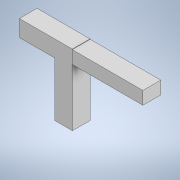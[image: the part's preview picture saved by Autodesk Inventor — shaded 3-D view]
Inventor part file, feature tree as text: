
AUTODESK INVENTOR PART (.ipt)
format: ipt  version: 2021.1 (Build 251245000, 245)  size: 110,592 bytes
history: native  units: in
note: dims shown in document units (in); Inventor stores cm internally (conversion verified against a paired STEP export)
features: extrude x3, sketch x3
ambient origin geometry x8: Origin, YZ Plane, XZ Plane, XY Plane, X Axis, Y Axis, Z Axis, Center Point
bodies: Solid1 (feature_tree)
feature tree (6):
  extrude  "Extrusion1"  Depth=4.0in TaperAngle=0.0deg
  extrude  "Extrusion2"  Depth=2.0in TaperAngle=0.0deg
  extrude  "Extrusion3"  [1 undecoded]
  sketch  "Sketch1"  dims[d0=1.0in d1=4.0in d2=0.0in]
  sketch  "Sketch2"  dims[d3=4.0in d4=0.0in d5=2.0in d6=0.0in]
  sketch  "Sketch3"
note: 1 required parameter value undecoded (feature->parameter linkage not recoverable at this tier; creation-order binding heuristic only, values carry confidence <= 0.55)
